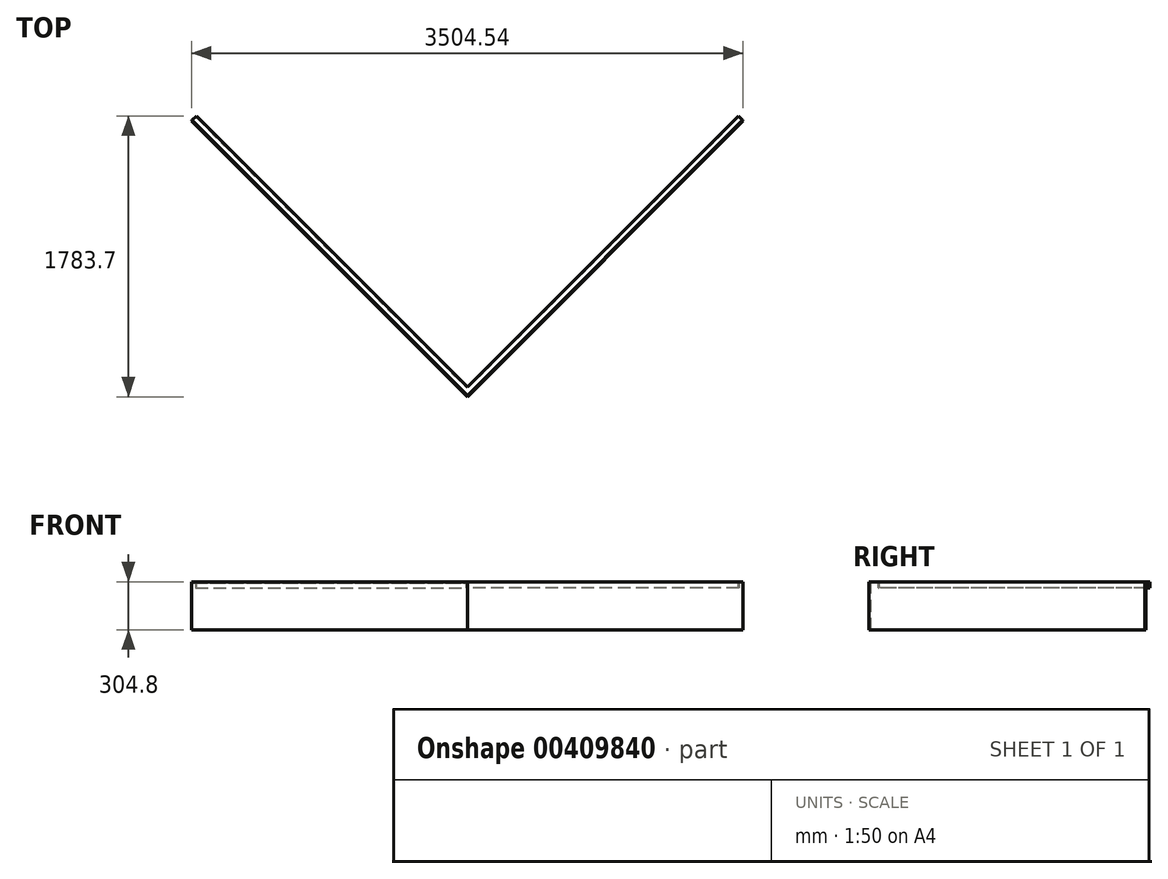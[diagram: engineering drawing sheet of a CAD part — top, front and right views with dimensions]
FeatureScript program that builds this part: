
annotation { "Feature Type Name" : "Feature", "Feature Type Description" : "" }
export const myFeature = defineFeature(function(context is Context, id is Id, definition is map)
    precondition{}
    {
        {
            var Q0;
            Q0=qCreatedBy(makeId("Top.planeOp"),FACE);
            var sketch = newSketch(context, id + "F0", { "sketchPlane" : qUnion([Q0])});
            skLineSegment(sketch, "E0", {"start": v(0, 0) * mm, "end": v(1752.27, 1752.27) * mm});
            skLineSegment(sketch, "E1", {"start": v(0, 0) * mm, "end": v(-1752.27, 1752.27) * mm});
            skLineSegment(sketch, "E2", {"start": v(-1752.27, 1752.27) * mm, "end": v(-1747.78, 1756.76) * mm});
            skLineSegment(sketch, "E3", {"start": v(-1747.78, 1756.76) * mm, "end": v(0, 8.98) * mm});
            skLineSegment(sketch, "E4", {"start": v(1752.27, 1752.27) * mm, "end": v(1747.78, 1756.76) * mm});
            skLineSegment(sketch, "E5", {"start": v(1747.78, 1756.76) * mm, "end": v(0, 8.98) * mm});
            skSolve(sketch);
        }
        {
            var Q0;
            Q0=makeQuery(id+"F0.imprint","IMPRINT",FACE,{"disambiguationData":[TD([[makeQuery(id+"F0.imprint","IMPRINT",EDGE,{"derivedFrom":sQuery(id+"F0.wireOp",EDGE,"E0")}),1.0]])]});
            extrude(context, id + "F1", {"entities" : qUnion([Q0]), "depth" : 304.8 * mm});
        }
        {
            var Q0;
            Q0=makeQuery(id+"F1.opExtrude","CAP_FACE",FACE,{"disambiguationData":[OSD([sQuery(id+"F0.wireOp",EDGE,"E0"),sQuery(id+"F0.wireOp",EDGE,"E1"),sQuery(id+"F0.wireOp",EDGE,"E2"),sQuery(id+"F0.wireOp",EDGE,"E3"),sQuery(id+"F0.wireOp",EDGE,"E4"),sQuery(id+"F0.wireOp",EDGE,"E5")])],"isStart":false});
            var sketch = newSketch(context, id + "F2", { "sketchPlane" : qUnion([Q0])});
            skLineSegment(sketch, "E6", {"start": v(-1747.78, 1756.76) * mm, "end": v(-1720.84, 1783.7) * mm});
            skLineSegment(sketch, "E7", {"start": v(-1720.84, 1783.7) * mm, "end": v(0, 62.86) * mm});
            skLineSegment(sketch, "E8", {"start": v(1747.78, 1756.76) * mm, "end": v(1720.84, 1783.7) * mm});
            skLineSegment(sketch, "E9", {"start": v(1720.84, 1783.7) * mm, "end": v(0, 62.86) * mm});
            skSolve(sketch);
        }
        {
            var Q0;
            Q0=makeQuery(id+"F2.imprint","IMPRINT",FACE,{"disambiguationData":[TD([[makeQuery(id+"F2.imprint","IMPRINT",EDGE,{"derivedFrom":sQuery(id+"F2.wireOp",EDGE,"E6")}),-1.0]])]});
            extrude(context, id + "F3", {"entities" : qUnion([Q0]), "depth" : -6.35 * mm});
        }
        {
            var Q0;
            Q0=makeQuery(id+"F3.opExtrude","SWEPT_FACE",FACE,{"disambiguationData":[OSD([sQuery(id+"F2.wireOp",EDGE,"E9")])]});
            var sketch = newSketch(context, id + "F4", { "sketchPlane" : qUnion([Q0])});
            skLineSegment(sketch, "E10", {"start": v(-2478.09, 304.8) * mm, "end": v(-44.45, 304.8) * mm});
            skLineSegment(sketch, "E11", {"start": v(-44.45, 304.8) * mm, "end": v(-44.45, 266.7) * mm});
            skLineSegment(sketch, "E12", {"start": v(-2478.09, 304.8) * mm, "end": v(-2478.09, 266.7) * mm});
            skLineSegment(sketch, "E13", {"start": v(-2478.09, 266.7) * mm, "end": v(-44.45, 266.7) * mm});
            skSolve(sketch);
        }
        {
            var Q0;
            {var subQ2=sQuery(id+"F4.wireOp",EDGE,"E13");Q0=makeQuery(id+"F4.imprint","IMPRINT",FACE,{"disambiguationData":[TD([[makeQuery(id+"F4.imprint","IMPRINT",EDGE,{"derivedFrom":subQ2}),1.0]])]});}
            extrude(context, id + "F5", {"entities" : qUnion([Q0]), "oppositeDirection" : true, "depth" : 6.35 * mm});
        }
        {
            var Q0;
            Q0=makeQuery(id+"F3.opExtrude","SWEPT_FACE",FACE,{"disambiguationData":[OSD([sQuery(id+"F2.wireOp",EDGE,"E7")])]});
            var sketch = newSketch(context, id + "F6", { "sketchPlane" : qUnion([Q0])});
            skLineSegment(sketch, "E14", {"start": v(2478.09, 304.8) * mm, "end": v(2478.09, 266.7) * mm});
            skLineSegment(sketch, "E15", {"start": v(2478.09, 266.7) * mm, "end": v(44.49, 266.7) * mm});
            skLineSegment(sketch, "E16", {"start": v(44.49, 266.7) * mm, "end": v(44.45, 298.45) * mm});
            skLineSegment(sketch, "E17", {"start": v(44.45, 298.45) * mm, "end": v(2478.09, 304.8) * mm});
            skSolve(sketch);
        }
        {
            var Q0;
            {var subQ2=sQuery(id+"F6.wireOp",EDGE,"E15");Q0=makeQuery(id+"F6.imprint","IMPRINT",FACE,{"disambiguationData":[TD([[makeQuery(id+"F6.imprint","IMPRINT",EDGE,{"derivedFrom":subQ2}),-1.0]])]});}
            extrude(context, id + "F7", {"entities" : qUnion([Q0]), "operationType" : NewBodyOperationType.ADD, "depth" : -6.35 * mm});
        }
    });
